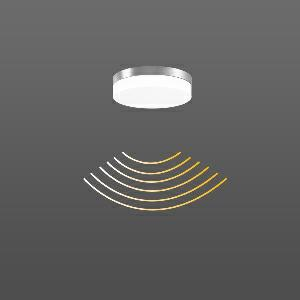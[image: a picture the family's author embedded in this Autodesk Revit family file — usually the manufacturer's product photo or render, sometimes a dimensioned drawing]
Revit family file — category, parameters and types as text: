
# Revit family: flat_slim_round_312135_004_2_19_22a0
name_source: partatom
category: Lighting Fixtures
units: mm (PartAtom-declared; Revit-internal decimal feet)

## family parameters
Cut with Voids When Loaded = No
Host = Face
Light Source = No
Part Type = Normal
Room Calculation Point = No
Round Connector Dimension = Use Diameter
Shared = No

## types (1)
- FLAT SLIM round (1 x LED Modul 830, 1300 lm, 3000)
    Apparent Load = 12 VA
    CIE Flux Codes = 43 74 92 91 100
    Color Rendering = 80
    Color Temperature = 3000
    Default Elevation = 1800 mm
    Height = 63 mm
    Lamp = 1 x LED Modul 830
    Lamp Light Flux = 1300 lm
    Lamp count = 1
    Length = 230 mm
    Lifetime = 50000 h
    Luminous efficacy = 108 lm/W
    Manufacturer = RZB
    ModVariant = No
    Model = 312135.004.2.19
    Mounting Place = Ceiling, Wall
    Mounting Type = Surface mounted
    Number of Poles = 1
    OnlyDefault = Yes
    Power Factor = 1
    Product Name = FLAT SLIM round
    Product group = Surface mounted ceiling and wall luminaires
    ProductGroupID = 305
    Protection Class = Protection class I
    Protection Degree = IP 65
    RLX_Detail_Level = 1
    RLX_Emergency_Light_Flux = 0 lm
    RLX_Emergency_Type = 0
    RLX_Emergency_Type_DB = No
    RlxData = <blob elided: 32165 chars, md5=7eddae24>
    Socket = socket
    Standby Power = 0 W
    System Light Flux = 1300 lm
    System Power = 12 W
    Type Comments = Product without accessories
    Type Image = 312132.004.19.jpg
    URL = http://relux.com
    VarID = ---
    Voltage = 230 V
    Voltage Range = 220-240 V
    Weight = 0.00 kg
    Width = 0 mm  [stored 0 ft]

note: [stored X ft] marks values corroborated as IEEE doubles in the binary element streams (Revit-internal decimal feet)

## geometry (parser evidence)
native form markers: Blend x4, Sweep x13
no freeform markers — native parametric forms only
